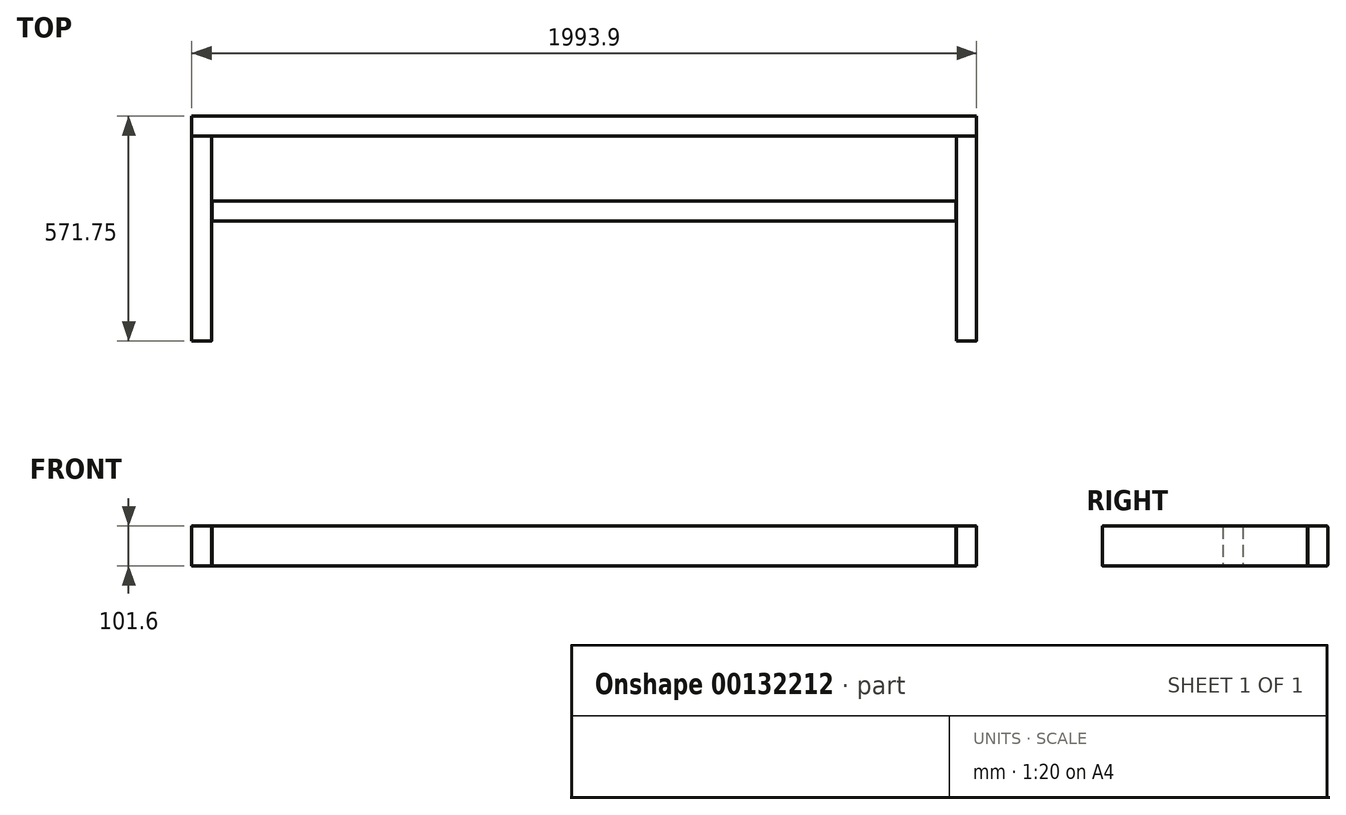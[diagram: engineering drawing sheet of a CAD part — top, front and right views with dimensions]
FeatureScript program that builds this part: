
annotation { "Feature Type Name" : "Feature", "Feature Type Description" : "" }
export const myFeature = defineFeature(function(context is Context, id is Id, definition is map)
    precondition{}
    {
        {
            var Q0;
            Q0=qCreatedBy(makeId("Front.planeOp"),FACE);
            var sketch = newSketch(context, id + "F0", { "sketchPlane" : qUnion([Q0])});
            skLineSegment(sketch, "E0.bottom", {"start": v(-996.95, -50.8) * mm, "end": v(996.95, -50.8) * mm});
            skLineSegment(sketch, "E0.top", {"start": v(-996.95, 50.8) * mm, "end": v(996.95, 50.8) * mm});
            skLineSegment(sketch, "E0.left", {"start": v(-996.95, -50.8) * mm, "end": v(-996.95, 50.8) * mm});
            skLineSegment(sketch, "E0.right", {"start": v(996.95, -50.8) * mm, "end": v(996.95, 50.8) * mm});
            skPoint(sketch, "E0.middle", {"position": v(0, 0) * mm});
            skSolve(sketch);
        }
        {
            var Q0;
            Q0 = qSketchRegion(id + "F0", true);
            extrude(context, id + "F1", {"entities" : qUnion([Q0]), "depth" : 50.8 * mm});
        }
        {
            var Q0;
            Q0=makeQuery(id+"F1.opExtrude","CAP_EDGE",EDGE,{"disambiguationData":[OSD([sQuery(id+"F0.wireOp",EDGE,"E0.bottom")])],"isStart":true});
            var Q1;
            Q1=makeQuery(id+"F1.opExtrude","CAP_EDGE",EDGE,{"disambiguationData":[OSD([sQuery(id+"F0.wireOp",EDGE,"E0.top")])],"isStart":true});
            var Q2;
            Q2=makeQuery(id+"F1.opExtrude","CAP_EDGE",EDGE,{"disambiguationData":[OSD([sQuery(id+"F0.wireOp",EDGE,"E0.bottom")])],"isStart":false});
            var Q3;
            Q3=makeQuery(id+"F1.opExtrude","CAP_EDGE",EDGE,{"disambiguationData":[OSD([sQuery(id+"F0.wireOp",EDGE,"E0.top")])],"isStart":false});
            fillet(context, id + "F2", {"entities" : qUnion([Q0, Q1, Q2, Q3]), "radius" : 2.54 * mm, "tangentPropagation" : true, "allowEdgeOverflow" : false});
        }
        {
            var Q0;
            Q0=qCreatedBy(makeId("Top.planeOp"),FACE);
            var sketch = newSketch(context, id + "F3", { "sketchPlane" : qUnion([Q0])});
            skLineSegment(sketch, "E1.bottom", {"start": v(-996.95, -51.05) * mm, "end": v(-946.15, -51.05) * mm});
            skLineSegment(sketch, "E1.top", {"start": v(-996.95, -571.75) * mm, "end": v(-946.15, -571.75) * mm});
            skLineSegment(sketch, "E1.left", {"start": v(-996.95, -51.05) * mm, "end": v(-996.95, -571.75) * mm});
            skLineSegment(sketch, "E1.right", {"start": v(-946.15, -51.05) * mm, "end": v(-946.15, -571.75) * mm});
            skSolve(sketch);
        }
        {
            var Q0;
            Q0=makeQuery(id+"F3.imprint","IMPRINT",FACE,{"disambiguationData":[TD([[makeQuery(id+"F3.imprint","IMPRINT",EDGE,{"derivedFrom":sQuery(id+"F3.wireOp",EDGE,"E1.bottom")}),-1.0]])]});
            extrude(context, id + "F4", {"entities" : qUnion([Q0]), "endBound" : BoundingType.SYMMETRIC, "depth" : 101.6 * mm});
        }
        {
            var Q0;
            Q0=makeQuery(id+"F4.opExtrude","CAP_EDGE",EDGE,{"disambiguationData":[OSD([sQuery(id+"F3.wireOp",EDGE,"E1.left")])],"isStart":false});
            var Q1;
            Q1=makeQuery(id+"F4.opExtrude","CAP_EDGE",EDGE,{"disambiguationData":[OSD([sQuery(id+"F3.wireOp",EDGE,"E1.right")])],"isStart":false});
            var Q2;
            Q2=makeQuery(id+"F4.opExtrude","CAP_EDGE",EDGE,{"disambiguationData":[OSD([sQuery(id+"F3.wireOp",EDGE,"E1.left")])],"isStart":true});
            var Q3;
            Q3=makeQuery(id+"F4.opExtrude","CAP_EDGE",EDGE,{"disambiguationData":[OSD([sQuery(id+"F3.wireOp",EDGE,"E1.right")])],"isStart":true});
            fillet(context, id + "F5", {"entities" : qUnion([Q0, Q1, Q2, Q3]), "radius" : 2.54 * mm, "tangentPropagation" : true, "allowEdgeOverflow" : false});
        }
        {
            var Q0;
            Q0=qCreatedBy(makeId("Top.planeOp"),FACE);
            var sketch = newSketch(context, id + "F6", { "sketchPlane" : qUnion([Q0])});
            skLineSegment(sketch, "E2.bottom", {"start": v(946.15, -51.05) * mm, "end": v(996.95, -51.05) * mm});
            skLineSegment(sketch, "E2.top", {"start": v(946.15, -571.75) * mm, "end": v(996.95, -571.75) * mm});
            skLineSegment(sketch, "E2.left", {"start": v(946.15, -51.05) * mm, "end": v(946.15, -571.75) * mm});
            skLineSegment(sketch, "E2.right", {"start": v(996.95, -51.05) * mm, "end": v(996.95, -571.75) * mm});
            skSolve(sketch);
        }
        {
            var Q0;
            Q0=makeQuery(id+"F6.imprint","IMPRINT",FACE,{"disambiguationData":[TD([[makeQuery(id+"F6.imprint","IMPRINT",EDGE,{"derivedFrom":sQuery(id+"F6.wireOp",EDGE,"E2.bottom")}),-1.0]])]});
            extrude(context, id + "F7", {"entities" : qUnion([Q0]), "endBound" : BoundingType.SYMMETRIC, "depth" : 101.6 * mm});
        }
        {
            var Q0;
            Q0=qCreatedBy(makeId("Top.planeOp"),FACE);
            var sketch = newSketch(context, id + "F8", { "sketchPlane" : qUnion([Q0])});
            skLineSegment(sketch, "E3.bottom", {"start": v(-945.9, -215.9) * mm, "end": v(943.86, -215.9) * mm});
            skLineSegment(sketch, "E3.top", {"start": v(-945.9, -266.7) * mm, "end": v(943.86, -266.7) * mm});
            skLineSegment(sketch, "E3.left", {"start": v(-945.9, -215.9) * mm, "end": v(-945.9, -266.7) * mm});
            skLineSegment(sketch, "E3.right", {"start": v(943.86, -215.9) * mm, "end": v(943.86, -266.7) * mm});
            skSolve(sketch);
        }
        {
            var Q0;
            Q0=makeQuery(id+"F8.imprint","IMPRINT",FACE,{"disambiguationData":[TD([[makeQuery(id+"F8.imprint","IMPRINT",EDGE,{"derivedFrom":sQuery(id+"F8.wireOp",EDGE,"E3.bottom")}),-1.0]])]});
            extrude(context, id + "F9", {"entities" : qUnion([Q0]), "operationType" : NewBodyOperationType.ADD, "endBound" : BoundingType.SYMMETRIC, "depth" : 101.6 * mm});
        }
        {
            var Q0;
            Q0=makeQuery(id+"F9.opExtrude","CAP_EDGE",EDGE,{"disambiguationData":[OSD([sQuery(id+"F8.wireOp",EDGE,"E3.bottom")])],"isStart":false});
            var Q1;
            Q1=makeQuery(id+"F9.opExtrude","CAP_EDGE",EDGE,{"disambiguationData":[OSD([sQuery(id+"F8.wireOp",EDGE,"E3.top")])],"isStart":false});
            var Q2;
            Q2=makeQuery(id+"F9.opExtrude","CAP_EDGE",EDGE,{"disambiguationData":[OSD([sQuery(id+"F8.wireOp",EDGE,"E3.top")])],"isStart":true});
            var Q3;
            Q3=makeQuery(id+"F7.opExtrude","CAP_EDGE",EDGE,{"disambiguationData":[OSD([sQuery(id+"F6.wireOp",EDGE,"E2.left")])],"isStart":true});
            var Q4;
            Q4=makeQuery(id+"F7.opExtrude","CAP_EDGE",EDGE,{"disambiguationData":[OSD([sQuery(id+"F6.wireOp",EDGE,"E2.left")])],"isStart":false});
            var Q5;
            Q5=makeQuery(id+"F7.opExtrude","CAP_EDGE",EDGE,{"disambiguationData":[OSD([sQuery(id+"F6.wireOp",EDGE,"E2.right")])],"isStart":false});
            var Q6;
            Q6=makeQuery(id+"F7.opExtrude","CAP_EDGE",EDGE,{"disambiguationData":[OSD([sQuery(id+"F6.wireOp",EDGE,"E2.right")])],"isStart":true});
            var Q7;
            Q7=makeQuery(id+"F9.opExtrude","CAP_EDGE",EDGE,{"disambiguationData":[OSD([sQuery(id+"F8.wireOp",EDGE,"E3.bottom")])],"isStart":true});
            fillet(context, id + "F10", {"entities" : qUnion([Q0, Q1, Q2, Q3, Q4, Q5, Q6, Q7]), "radius" : 2.54 * mm, "tangentPropagation" : true, "allowEdgeOverflow" : false});
        }
    });
